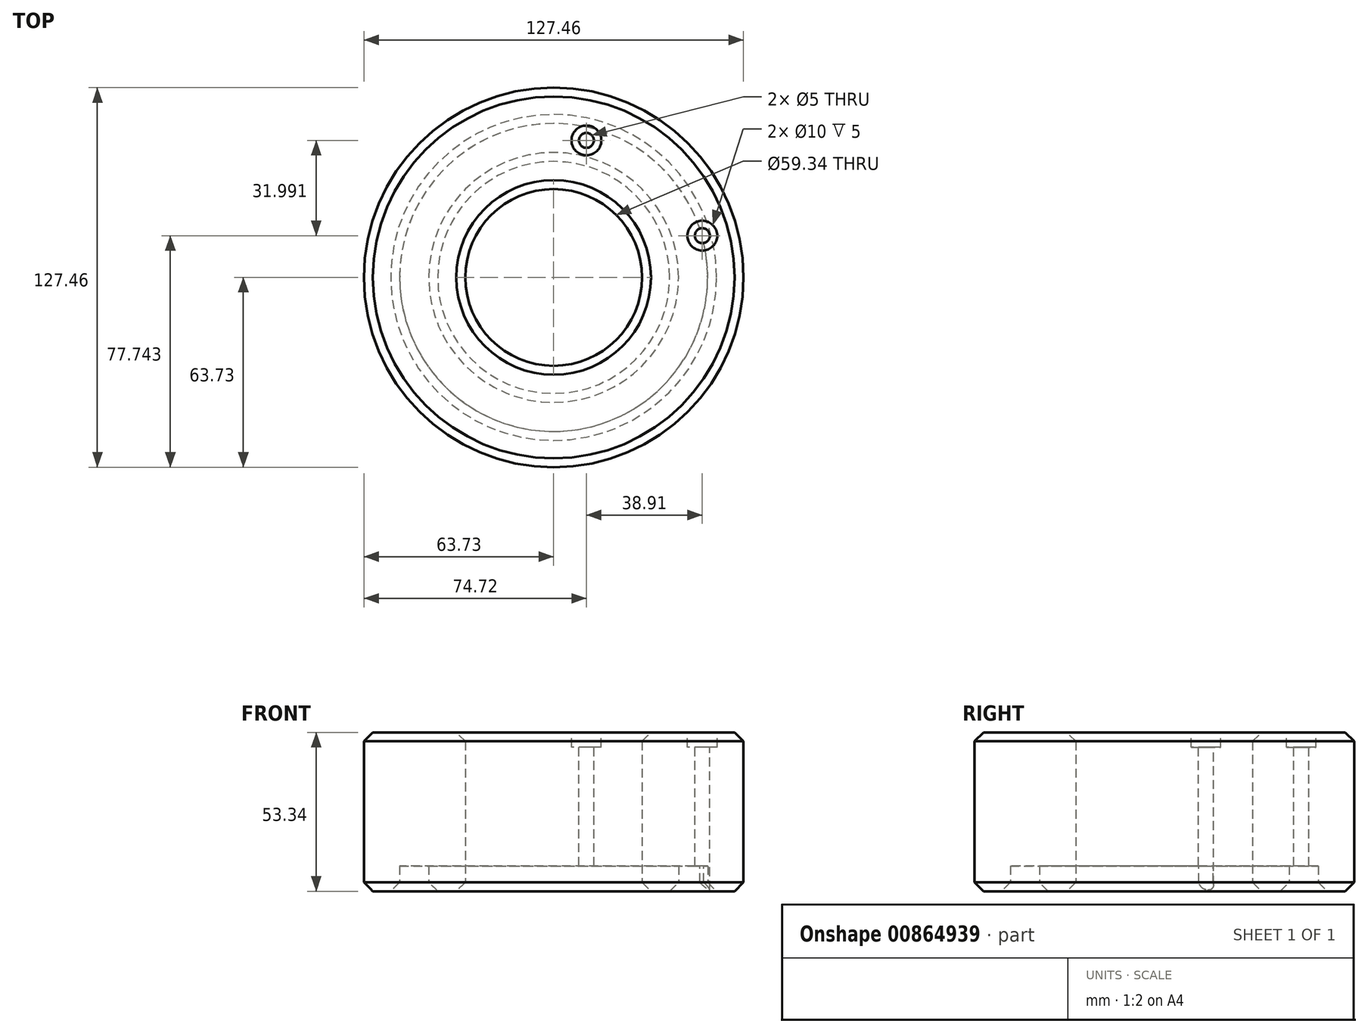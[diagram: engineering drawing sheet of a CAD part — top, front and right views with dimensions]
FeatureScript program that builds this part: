
annotation { "Feature Type Name" : "Feature", "Feature Type Description" : "" }
export const myFeature = defineFeature(function(context is Context, id is Id, definition is map)
    precondition{}
    {
        {
            var Q0;
            Q0=qCreatedBy(makeId("Right.planeOp"),FACE);
            var sketch = newSketch(context, id + "F0", { "sketchPlane" : qUnion([Q0])});
            skLineSegment(sketch, "E0", {"start": v(0, 0) * mm, "end": v(0, 28.04) * mm, "construction": true});
            skLineSegment(sketch, "E1", {"start": v(29.67, 30.55) * mm, "end": v(29.67, -22.79) * mm});
            skLineSegment(sketch, "E2", {"start": v(29.67, -22.79) * mm, "end": v(41.94, -22.79) * mm});
            skLineSegment(sketch, "E3", {"start": v(41.94, -22.79) * mm, "end": v(41.94, -14.27) * mm});
            skLineSegment(sketch, "E4", {"start": v(41.94, -14.27) * mm, "end": v(51.7, -14.27) * mm});
            skLineSegment(sketch, "E5", {"start": v(51.7, -14.27) * mm, "end": v(51.7, -22.79) * mm});
            skLineSegment(sketch, "E6", {"start": v(51.7, -22.79) * mm, "end": v(63.73, -22.79) * mm});
            skLineSegment(sketch, "E7", {"start": v(63.73, -22.79) * mm, "end": v(63.73, 30.55) * mm});
            skLineSegment(sketch, "E8", {"start": v(63.73, 30.55) * mm, "end": v(29.67, 30.55) * mm});
            skSolve(sketch);
        }
        {
            var Q0;
            Q0=makeQuery(id+"F0.imprint","IMPRINT",FACE,{"disambiguationData":[TD([[makeQuery(id+"F0.imprint","IMPRINT",EDGE,{"derivedFrom":sQuery(id+"F0.wireOp",EDGE,"E1")}),1.0]])]});
            var Q1;
            Q1=sQuery(id+"F0.wireOp",EDGE,"E0");
            revolve(context, id + "F1", {"surfaceOperationType" : NewSurfaceOperationType.NEW, "entities" : qUnion([Q0]), "axis" : qUnion([Q1]), "revolveType" : RevolveType.FULL});
        }
        {
            var Q0;
            Q0=makeQuery(id+"F1.opRevolve","SWEPT_FACE",FACE,{"disambiguationData":[OSD([sQuery(id+"F0.wireOp",EDGE,"E8")])]});
            var sketch = newSketch(context, id + "F2", { "sketchPlane" : qUnion([Q0])});
            skPoint(sketch, "E9", {"position": v(11, 46) * mm});
            skPoint(sketch, "E10", {"position": v(49.9, 14.01) * mm});
            skSolve(sketch);
        }
        {
            var Q0;
            Q0=sQuery(id+"F2.wireOp",VERTEX,"E9");
            var Q1;
            Q1=sQuery(id+"F2.wireOp",VERTEX,"E10");
            var Q2;
            Q2=makeQuery(id+"F1.opRevolve","SWEPT_BODY",BODY,{"disambiguationData":[OSD([sQuery(id+"F0.wireOp",EDGE,"E1"),sQuery(id+"F0.wireOp",EDGE,"E2"),sQuery(id+"F0.wireOp",EDGE,"E3"),sQuery(id+"F0.wireOp",EDGE,"E4"),sQuery(id+"F0.wireOp",EDGE,"E5"),sQuery(id+"F0.wireOp",EDGE,"E6"),sQuery(id+"F0.wireOp",EDGE,"E7"),sQuery(id+"F0.wireOp",EDGE,"E8")])]});
            hole(context, id + "F3", {"style" : HoleStyle.C_BORE, "endStyle" : HoleEndStyle.THROUGH, "holeDiameter" : 5 * mm, "cBoreDiameter" : 10 * mm, "cBoreDepth" : 5 * mm, "majorDiameter" : 5 * mm, "isTappedThrough" : true, "tappedDepth" : 12 * mm, "tapClearance" : 3, "locations" : qUnion([Q0, Q1]), "scope" : qUnion([Q2])});
        }
        {
            var Q0;
            Q0=makeQuery(id+"F1.opRevolve","SWEPT_EDGE",EDGE,{"disambiguationData":[OSD([sQuery(id+"F0.wireOp",EDGE,"E7"),sQuery(id+"F0.wireOp",EDGE,"E8")])]});
            var Q1;
            Q1=makeQuery(id+"F1.opRevolve","SWEPT_EDGE",EDGE,{"disambiguationData":[OSD([sQuery(id+"F0.wireOp",EDGE,"E6"),sQuery(id+"F0.wireOp",EDGE,"E7")])]});
            var Q2;
            Q2=makeQuery(id+"F1.opRevolve","SWEPT_EDGE",EDGE,{"disambiguationData":[OSD([sQuery(id+"F0.wireOp",EDGE,"E5"),sQuery(id+"F0.wireOp",EDGE,"E6")])]});
            var Q3;
            Q3=makeQuery(id+"F1.opRevolve","SWEPT_EDGE",EDGE,{"disambiguationData":[OSD([sQuery(id+"F0.wireOp",EDGE,"E2"),sQuery(id+"F0.wireOp",EDGE,"E3")])]});
            var Q4;
            Q4=makeQuery(id+"F1.opRevolve","SWEPT_EDGE",EDGE,{"disambiguationData":[OSD([sQuery(id+"F0.wireOp",EDGE,"E1"),sQuery(id+"F0.wireOp",EDGE,"E2")])]});
            var Q5;
            Q5=makeQuery(id+"F1.opRevolve","SWEPT_EDGE",EDGE,{"disambiguationData":[OSD([sQuery(id+"F0.wireOp",EDGE,"E1"),sQuery(id+"F0.wireOp",EDGE,"E8")])]});
            chamfer(context, id + "F4", {"entities" : qUnion([Q0, Q1, Q2, Q3, Q4, Q5]), "width" : 3 * mm, "tangentPropagation" : true});
        }
    });
